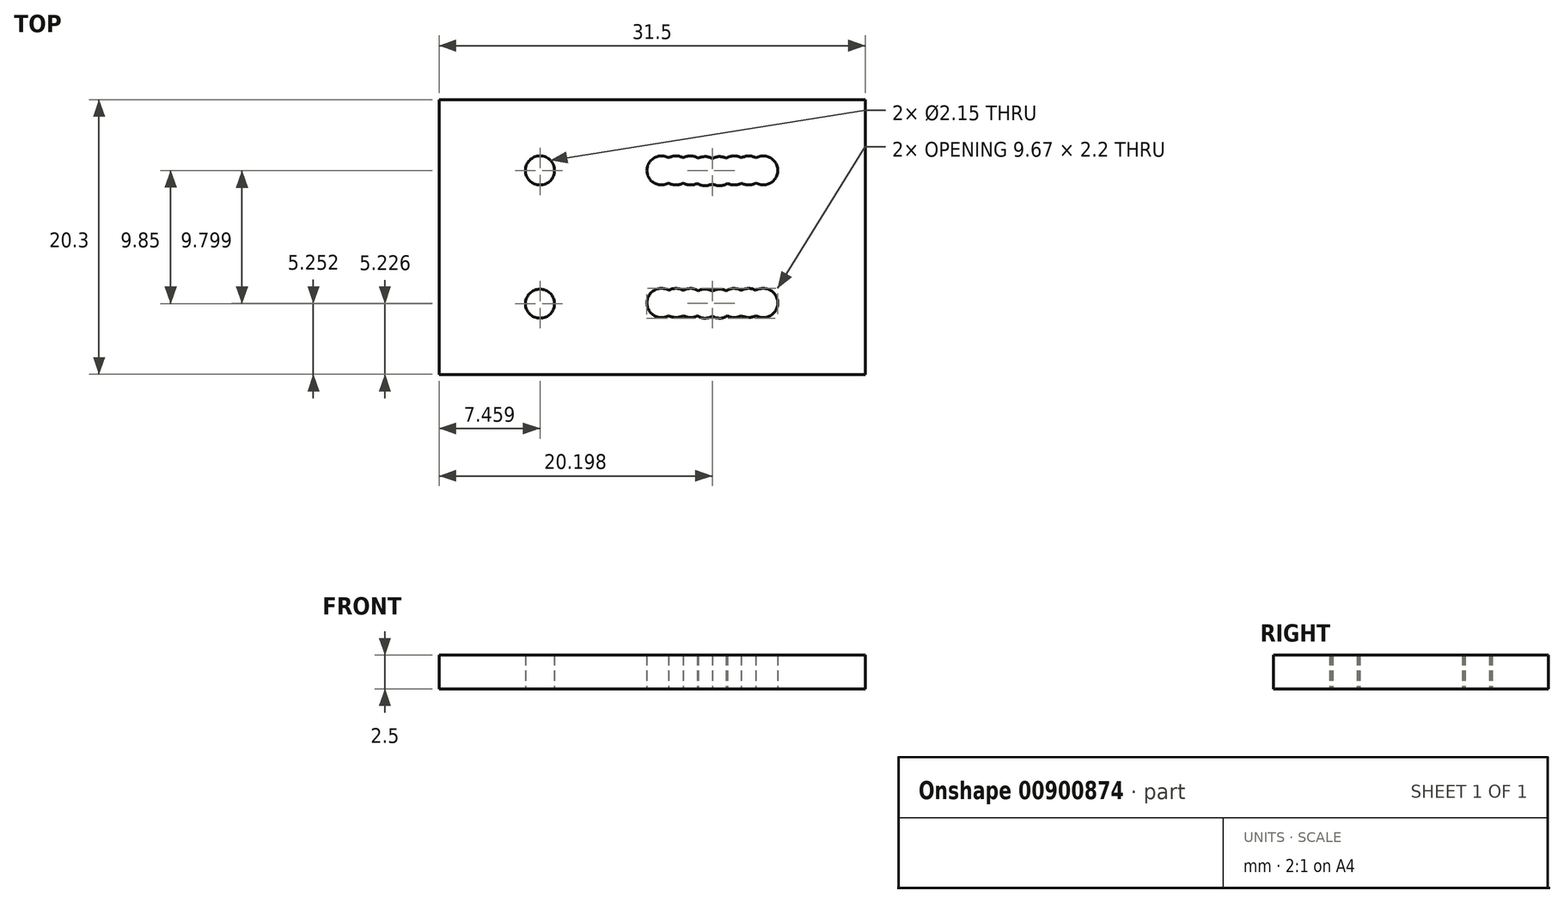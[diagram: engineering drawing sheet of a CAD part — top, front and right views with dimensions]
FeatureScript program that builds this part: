
annotation { "Feature Type Name" : "Feature", "Feature Type Description" : "" }
export const myFeature = defineFeature(function(context is Context, id is Id, definition is map)
    precondition{}
    {
        {
            var Q0;
            Q0=qCreatedBy(makeId("Top.planeOp"),FACE);
            var sketch = newSketch(context, id + "F0", { "sketchPlane" : qUnion([Q0])});
            skLineSegment(sketch, "E0.bottom", {"start": v(-17.48, 7.68) * mm, "end": v(14.02, 7.68) * mm});
            skLineSegment(sketch, "E0.top", {"start": v(-17.48, -12.62) * mm, "end": v(14.02, -12.62) * mm});
            skLineSegment(sketch, "E0.left", {"start": v(-17.48, 7.68) * mm, "end": v(-17.48, -12.62) * mm});
            skLineSegment(sketch, "E0.right", {"start": v(14.02, 7.68) * mm, "end": v(14.02, -12.62) * mm});
            skCircle(sketch, "E1", {"center": v(6.48, 2.46) * mm, "radius": 1.07 * mm});
            skCircle(sketch, "E2", {"center": v(6.48, -7.34) * mm, "radius": 1.07 * mm});
            skCircle(sketch, "E3", {"center": v(-10.02, 2.46) * mm, "radius": 1.07 * mm});
            skCircle(sketch, "E4", {"center": v(-10.02, -7.4) * mm, "radius": 1.07 * mm});
            skCircle(sketch, "E5", {"center": v(5.4, 2.46) * mm, "radius": 1.07 * mm});
            skCircle(sketch, "E6", {"center": v(5.4, -7.34) * mm, "radius": 1.07 * mm});
            skCircle(sketch, "E7", {"center": v(4.33, 2.46) * mm, "radius": 1.07 * mm});
            skCircle(sketch, "E8", {"center": v(4.33, -7.34) * mm, "radius": 1.07 * mm});
            skCircle(sketch, "E9", {"center": v(3.26, 2.4) * mm, "radius": 1.07 * mm});
            skCircle(sketch, "E10", {"center": v(3.26, -7.4) * mm, "radius": 1.07 * mm});
            skCircle(sketch, "E11", {"center": v(2.18, 2.4) * mm, "radius": 1.07 * mm});
            skCircle(sketch, "E12", {"center": v(2.18, -7.4) * mm, "radius": 1.07 * mm});
            skCircle(sketch, "E13", {"center": v(1.1, 2.46) * mm, "radius": 1.07 * mm});
            skCircle(sketch, "E14", {"center": v(1.1, -7.34) * mm, "radius": 1.07 * mm});
            skCircle(sketch, "E15", {"center": v(0.03, 2.46) * mm, "radius": 1.07 * mm});
            skCircle(sketch, "E16", {"center": v(0.03, -7.34) * mm, "radius": 1.07 * mm});
            skCircle(sketch, "E17", {"center": v(-1.04, 2.46) * mm, "radius": 1.07 * mm});
            skCircle(sketch, "E18", {"center": v(-1.04, -7.34) * mm, "radius": 1.07 * mm});
            skSolve(sketch);
        }
        {
            var Q0;
            Q0 = qSketchRegion(id + "F0", true);
            extrude(context, id + "F1", {"entities" : qUnion([Q0]), "depth" : 2.5 * mm, "offsetDistance" : 25 * mm});
        }
    });
